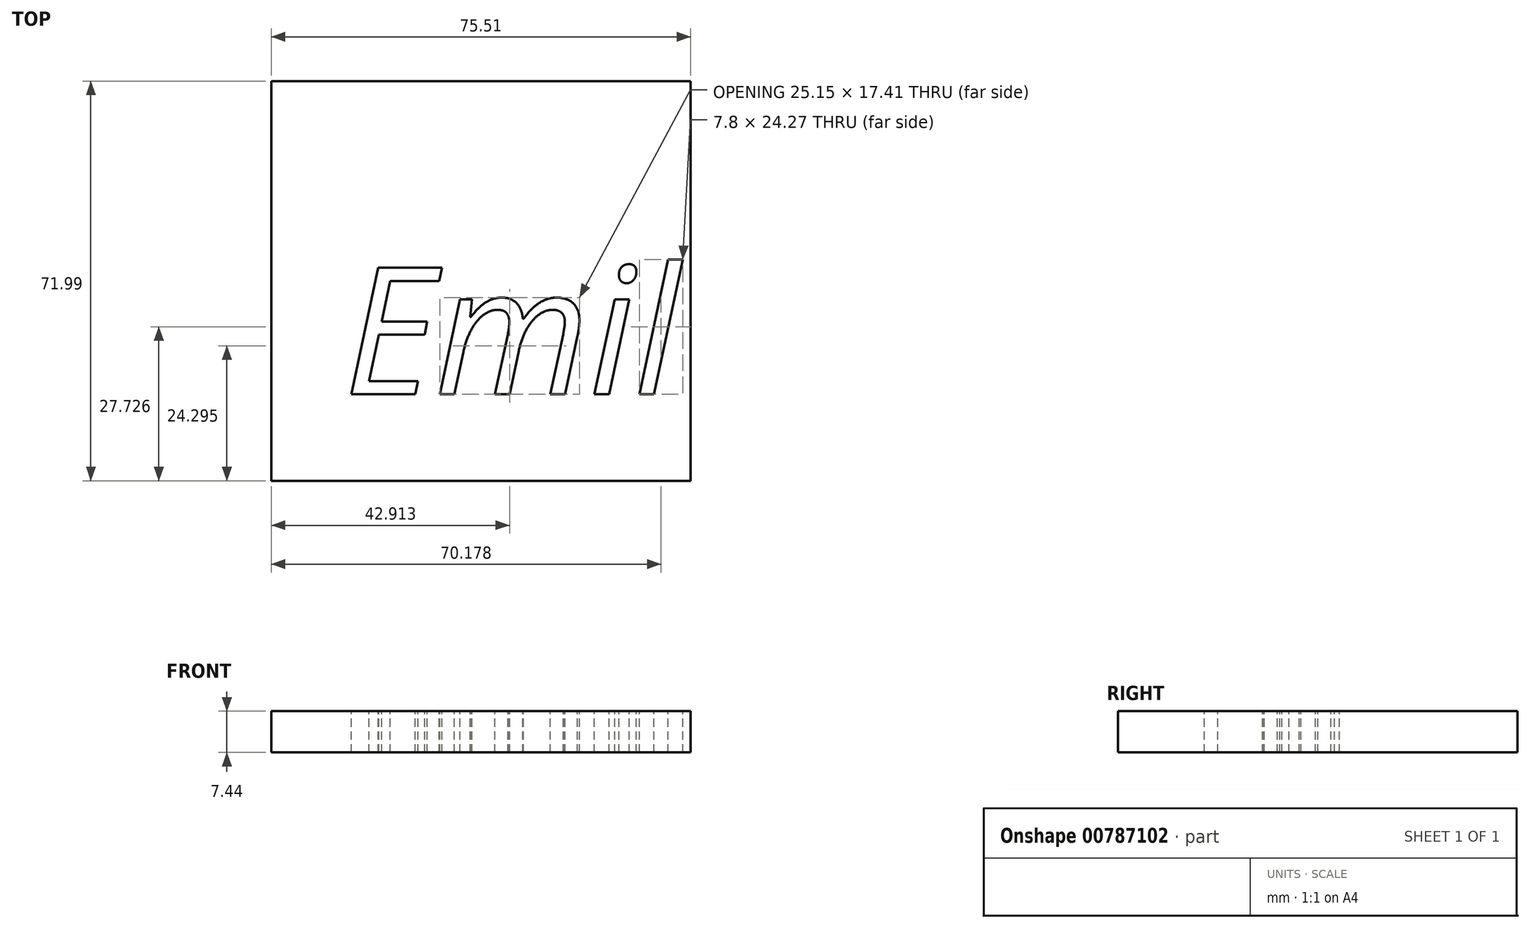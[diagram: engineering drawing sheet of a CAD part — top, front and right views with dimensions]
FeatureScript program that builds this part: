
annotation { "Feature Type Name" : "Feature", "Feature Type Description" : "" }
export const myFeature = defineFeature(function(context is Context, id is Id, definition is map)
    precondition{}
    {
        {
            var Q0;
            Q0=qCreatedBy(makeId("Top.planeOp"),FACE);
            var sketch = newSketch(context, id + "F0", { "sketchPlane" : qUnion([Q0])});
            skLineSegment(sketch, "E0.bottom", {"start": v(0, 71.99) * mm, "end": v(75.51, 71.99) * mm});
            skLineSegment(sketch, "E0.top", {"start": v(0, 0) * mm, "end": v(75.51, 0) * mm});
            skLineSegment(sketch, "E0.left", {"start": v(0, 71.99) * mm, "end": v(0, 0) * mm});
            skLineSegment(sketch, "E0.right", {"start": v(75.51, 71.99) * mm, "end": v(75.51, 0) * mm});
            skSolve(sketch);
        }
        {
            var Q0;
            Q0 = qSketchRegion(id + "F0", true);
            extrude(context, id + "F1", {"entities" : qUnion([Q0]), "depth" : 7.44 * mm, "offsetDistance" : 25.4 * mm});
        }
        {
            var Q0;
            Q0=makeQuery(id+"F1.opExtrude","CAP_FACE",FACE,{"disambiguationData":[OSD([sQuery(id+"F0.wireOp",EDGE,"E0.bottom"),sQuery(id+"F0.wireOp",EDGE,"E0.top"),sQuery(id+"F0.wireOp",EDGE,"E0.left"),sQuery(id+"F0.wireOp",EDGE,"E0.right")])],"isStart":false});
            var sketch = newSketch(context, id + "F2", { "sketchPlane" : qUnion([Q0])});
            skText(sketch, "E1", { "text": "Emil", "fontName": "OpenSans-Italic.ttf"});
            skText(sketch, "E2", { "text": "Default text", "fontName": "OpenSans-Regular.ttf"});
            const initialGuessF2  = {"E1": [0.01309, 0.01559, 1, 0, 0.023], "E2": [0.0709, 0.04227, 1, 0, 0.00069]};
            skSetInitialGuess(sketch, initialGuessF2);
            skSolve(sketch);
        }
        {
            var Q0;
            Q0=makeQuery(id+"F2.imprint","IMPRINT",FACE,{"disambiguationData":[TD([[makeQuery(id+"F2.imprint","IMPRINT",EDGE,{"derivedFrom":sQuery(id+"F2.wireOp",EDGE,"E1.sketch_text.stroke-12")}),-1.0]])]});
            var Q1;
            Q1=makeQuery(id+"F2.imprint","IMPRINT",FACE,{"disambiguationData":[TD([[makeQuery(id+"F2.imprint","IMPRINT",EDGE,{"derivedFrom":sQuery(id+"F2.wireOp",EDGE,"E1.sketch_text.stroke-0")}),-1.0]])]});
            var Q2;
            Q2=makeQuery(id+"F2.imprint","IMPRINT",FACE,{"disambiguationData":[TD([[makeQuery(id+"F2.imprint","IMPRINT",EDGE,{"derivedFrom":sQuery(id+"F2.wireOp",EDGE,"E1.sketch_text.stroke-46")}),-1.0]])]});
            var Q3;
            Q3=makeQuery(id+"F2.imprint","IMPRINT",FACE,{"disambiguationData":[TD([[makeQuery(id+"F2.imprint","IMPRINT",EDGE,{"derivedFrom":sQuery(id+"F2.wireOp",EDGE,"E1.sketch_text.stroke-50")}),-1.0]])]});
            var Q4;
            Q4=makeQuery(id+"F2.imprint","IMPRINT",FACE,{"disambiguationData":[TD([[makeQuery(id+"F2.imprint","IMPRINT",EDGE,{"derivedFrom":sQuery(id+"F2.wireOp",EDGE,"E1.sketch_text.stroke-57")}),-1.0]])]});
            extrude(context, id + "F3", {"entities" : qUnion([Q0, Q1, Q2, Q3, Q4]), "operationType" : NewBodyOperationType.REMOVE, "oppositeDirection" : true, "depth" : 25.4 * mm, "offsetDistance" : 25.4 * mm});
        }
        {
            var Q0;
            Q0=makeQuery(id+"F1.opExtrude","CAP_FACE",FACE,{"disambiguationData":[OSD([sQuery(id+"F0.wireOp",EDGE,"E0.bottom"),sQuery(id+"F0.wireOp",EDGE,"E0.top"),sQuery(id+"F0.wireOp",EDGE,"E0.left"),sQuery(id+"F0.wireOp",EDGE,"E0.right")])],"isStart":false});
            var sketch = newSketch(context, id + "F4", { "sketchPlane" : qUnion([Q0])});
            skLineSegment(sketch, "E3", {"start": v(11.24, 0) * mm, "end": v(11.24, 77.58) * mm});
            skLineSegment(sketch, "E4", {"start": v(11.24, 77.58) * mm, "end": v(11.24, 71.99) * mm});
            skLineSegment(sketch, "E5", {"start": v(11.24, 71.99) * mm, "end": v(0, 71.99) * mm});
            skLineSegment(sketch, "E6", {"start": v(0, 71.99) * mm, "end": v(0, 56.2) * mm});
            skLineSegment(sketch, "E7", {"start": v(0, 56.2) * mm, "end": v(0, 50.63) * mm});
            skLineSegment(sketch, "E8", {"start": v(0, 50.63) * mm, "end": v(75.51, 50.63) * mm});
            skLineSegment(sketch, "E9", {"start": v(75.51, 50.63) * mm, "end": v(92.29, 38.55) * mm});
            skLineSegment(sketch, "E10", {"start": v(92.29, 38.55) * mm, "end": v(75.51, 50.63) * mm});
            skSolve(sketch);
        }
    });
